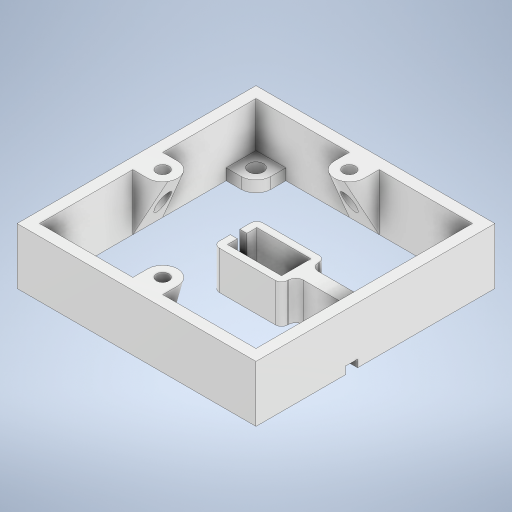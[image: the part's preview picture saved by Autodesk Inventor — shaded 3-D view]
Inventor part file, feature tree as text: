
AUTODESK INVENTOR PART (.ipt)
format: ipt  version: 2024 (Build 280153000, 153)  size: 479,744 bytes
history: native  units: in
note: dims shown in document units (in); Inventor stores cm internally (conversion verified against a paired STEP export)
features: sketch x9, extrude x6, pattern_circular x2, fillet x2, plane x2, projected_geometry x2, other x1, loft x1, hole x1
ambient origin geometry x8: Origin, YZ Plane, XZ Plane, XY Plane, X Axis, Y Axis, Z Axis, Center Point
bodies: Body1 (feature_tree)
feature tree (26):
  extrude  "Extrusion3"  Depth=4.0in
  extrude  "Extrusion4"  Depth=0.1875in TaperAngle=0.0deg
  pattern_circular  "Circular Pattern1"  Count=4 Angle=360.0deg
  sketch  "Sketch5"  dims[d22=4.0in]
  other  "Work Axis1"
  loft  "Loft1"
  hole  "Hole2"  [1 undecoded]
  pattern_circular  "Circular Pattern2"  [2 undecoded]
  extrude  "Extrusion11"  Depth=0.25in
  extrude  "Extrusion12"  TaperAngle=0.0deg  [1 undecoded]
  extrude  "Extrusion13"  Depth=0.5in TaperAngle=180.0deg
  extrude  "Extrusion14"  Depth=0.2in
  fillet  "Fillet11"  Radius=0.125in
  fillet  "Fillet12"  Radius=0.2in
  sketch  "Sketch3"  dims[d17=4.0in d18=4.0in]
  sketch  "Sketch4"  dims[d19=0.1875in d20=0.9419in d21=0.0in]
  plane  "Work Plane2"
  plane  "Work Plane3"
  sketch  "Sketch11"  dims[d23=4.0in]
  projected_geometry  "Projected Loop3"
  sketch  "Sketch12"  dims[d24=0.1875in]
  sketch  "Sketch13"  dims[d25=0.25in]
  projected_geometry  "Projected Loop5"
  sketch  "Sketch14"  dims[d26=0.125in]
  sketch  "Sketch15"  dims[d27=0.1875in d28=0.0in d30=1.5748in d31=360.0deg]
  sketch  "Sketch16"  dims[d35=3.625in d75=0.25in d98=0.5in d99=0.5in d100=0.25in d101=0.0in d102=90.0deg d103=0.0in d104=90.0deg d105=0.21in d106=0.75in d107=0.375in d108=0.25in d109=0.5635in d110=1.0in d111=0.8108in d112=1.1811in d113=180.0deg d115=0.2in d116=0.125in d117=0.2in d118=0.0in d119=0.4803in d120=0.8937in d121=0.2264in d122=0.125in d123=0.125in d124=0.125in d125=0.1in d126=0.125in d127=0.125in d128=0.6437in d129=0.0in d130=0.1575in d131=0.4375in d132=0.0in d133=0.9055in d134=0.4921in d135=0.8125in d136=0.0in d137=0.125in d138=0.1in d16=0.0312in d83=0.5in d84=0.0344in d85=0.5in d86=0.0344in]
note: 4 required parameter values undecoded (feature->parameter linkage not recoverable at this tier; creation-order binding heuristic only, values carry confidence <= 0.55)
